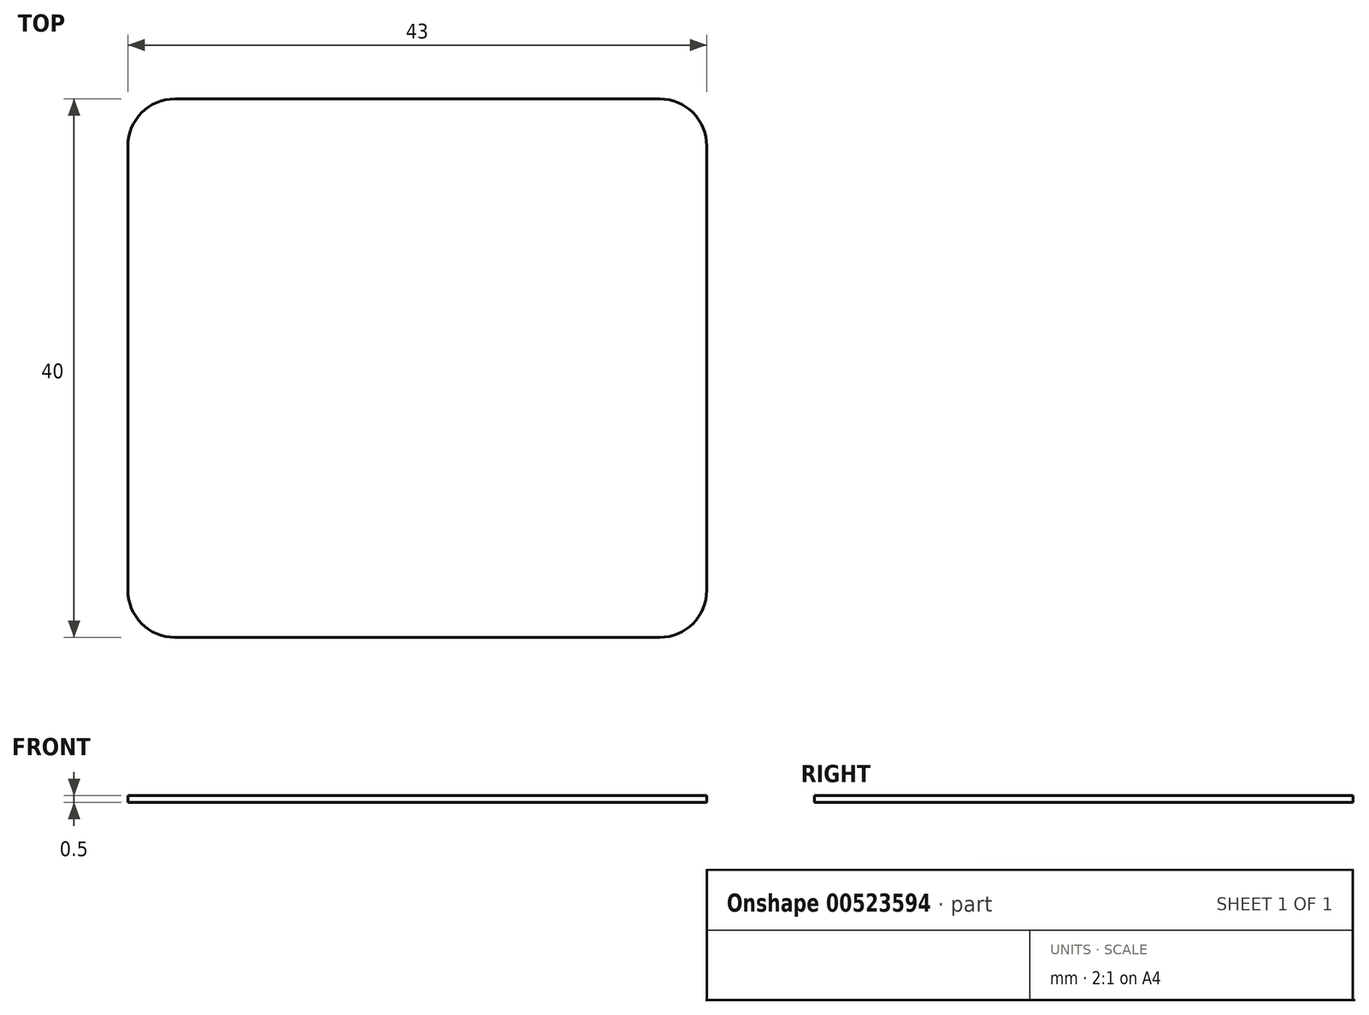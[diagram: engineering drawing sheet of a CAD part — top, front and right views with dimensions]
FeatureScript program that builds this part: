
annotation { "Feature Type Name" : "Feature", "Feature Type Description" : "" }
export const myFeature = defineFeature(function(context is Context, id is Id, definition is map)
    precondition{}
    {
        {
            var Q0;
            Q0=qCreatedBy(makeId("Top.planeOp"),FACE);
            var sketch = newSketch(context, id + "F0", { "sketchPlane" : qUnion([Q0])});
            skLineSegment(sketch, "E0.bottom", {"start": v(18, -20) * mm, "end": v(-18, -20) * mm});
            skLineSegment(sketch, "E0.top", {"start": v(18, 20) * mm, "end": v(-18, 20) * mm});
            skLineSegment(sketch, "E0.left", {"start": v(21.5, -16.5) * mm, "end": v(21.5, 16.5) * mm});
            skLineSegment(sketch, "E0.right", {"start": v(-21.5, -16.5) * mm, "end": v(-21.5, 16.5) * mm});
            skPoint(sketch, "E0.middle", {"position": v(0, 0) * mm});
            skPoint(sketch, "E1.visualSharp", {"position": v(-21.5, -20) * mm});
            skArc(sketch, "E1.filletArc", {"start": v(-21.5, -16.5) * mm, "mid": v(-20.47, -18.97) * mm, "end": v(-18, -20) * mm});
            skPoint(sketch, "E2.visualSharp", {"position": v(21.5, -20) * mm});
            skArc(sketch, "E2.filletArc", {"start": v(18, -20) * mm, "mid": v(20.47, -18.97) * mm, "end": v(21.5, -16.5) * mm});
            skPoint(sketch, "E3.visualSharp", {"position": v(21.5, 20) * mm});
            skArc(sketch, "E3.filletArc", {"start": v(21.5, 16.5) * mm, "mid": v(20.47, 18.97) * mm, "end": v(18, 20) * mm});
            skPoint(sketch, "E4.visualSharp", {"position": v(-21.5, 20) * mm});
            skArc(sketch, "E4.filletArc", {"start": v(-18, 20) * mm, "mid": v(-20.47, 18.97) * mm, "end": v(-21.5, 16.5) * mm});
            skSolve(sketch);
        }
        {
            var Q0;
            Q0=makeQuery(id+"F0.imprint","IMPRINT",FACE,{"disambiguationData":[TD([[makeQuery(id+"F0.imprint","IMPRINT",EDGE,{"derivedFrom":sQuery(id+"F0.wireOp",EDGE,"E0.bottom")}),-1.0]])]});
            extrude(context, id + "F1", {"entities" : qUnion([Q0]), "depth" : .5 * mm, "offsetDistance" : 25 * mm});
        }
    });
